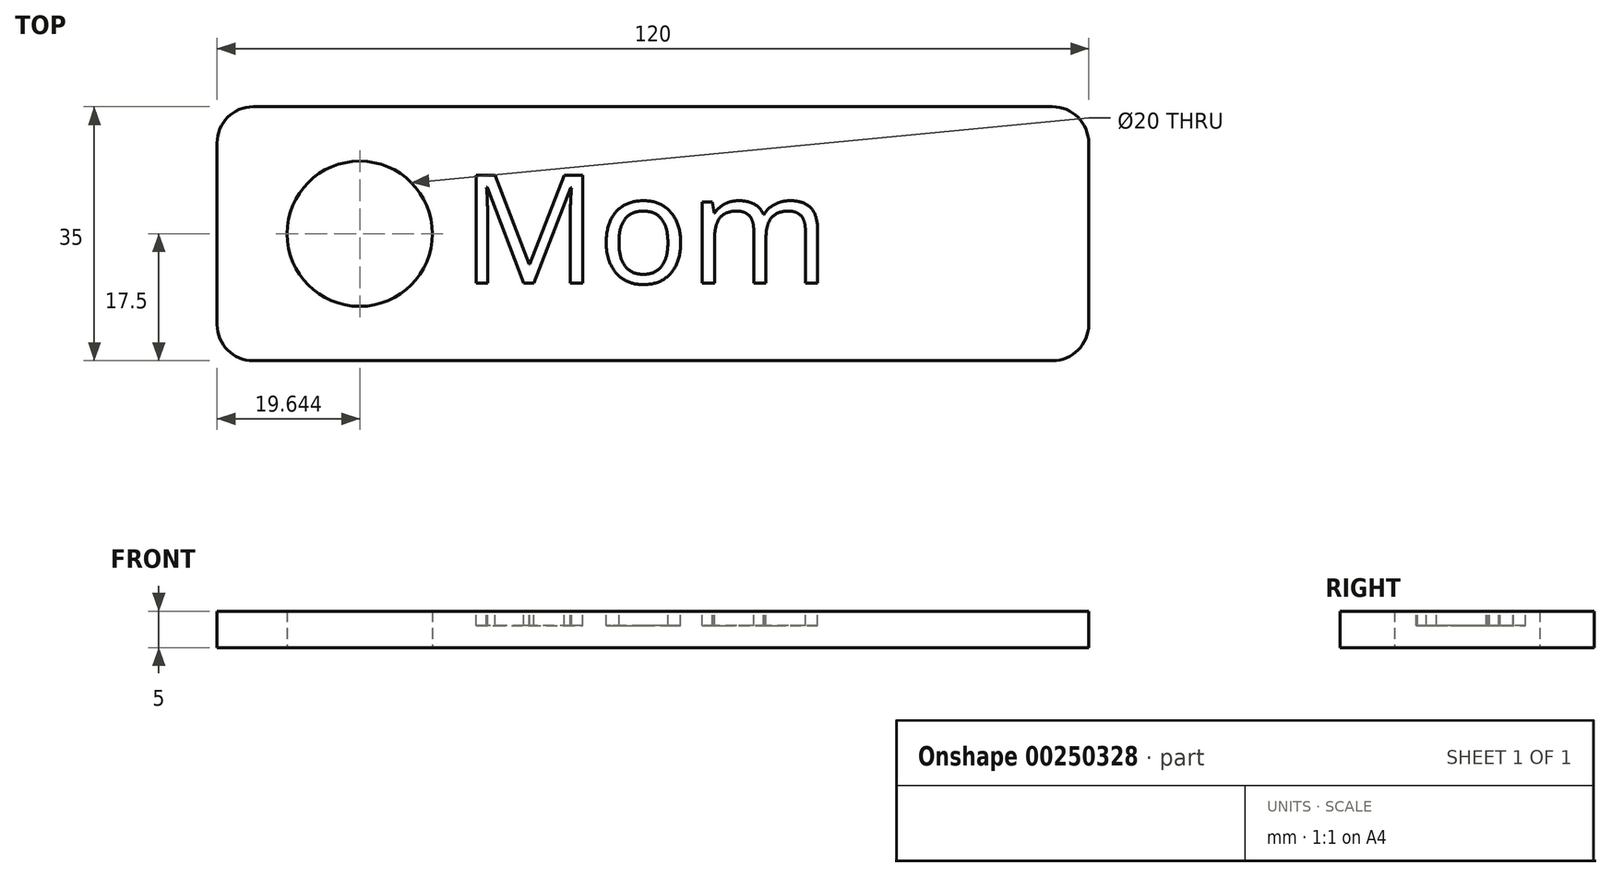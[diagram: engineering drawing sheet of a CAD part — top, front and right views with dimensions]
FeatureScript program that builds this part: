
annotation { "Feature Type Name" : "Feature", "Feature Type Description" : "" }
export const myFeature = defineFeature(function(context is Context, id is Id, definition is map)
    precondition{}
    {
        {
            var Q0;
            Q0=qCreatedBy(makeId("Top.planeOp"),FACE);
            var sketch = newSketch(context, id + "F0", { "sketchPlane" : qUnion([Q0])});
            skLineSegment(sketch, "E0.bottom", {"start": v(-60, 17.5) * mm, "end": v(60, 17.5) * mm});
            skLineSegment(sketch, "E0.top", {"start": v(-60, -17.5) * mm, "end": v(60, -17.5) * mm});
            skLineSegment(sketch, "E0.left", {"start": v(-60, 17.5) * mm, "end": v(-60, -17.5) * mm});
            skLineSegment(sketch, "E0.right", {"start": v(60, 17.5) * mm, "end": v(60, -17.5) * mm});
            skPoint(sketch, "E0.middle", {"position": v(0, 0) * mm});
            skCircle(sketch, "E1", {"center": v(-40.36, 0) * mm, "radius": 10 * mm});
            skSolve(sketch);
        }
        {
            var Q0;
            Q0=makeQuery(id+"F0.imprint","IMPRINT",FACE,{"disambiguationData":[TD([[makeQuery(id+"F0.imprint","IMPRINT",EDGE,{"derivedFrom":sQuery(id+"F0.wireOp",EDGE,"E0.bottom")}),-1.0]])]});
            extrude(context, id + "F1", {"entities" : qUnion([Q0]), "depth" : 5 * mm});
        }
        {
            var Q0;
            Q0=makeQuery(id+"F1.opExtrude","SWEPT_EDGE",EDGE,{"disambiguationData":[OSD([sQuery(id+"F0.wireOp",EDGE,"E0.top"),sQuery(id+"F0.wireOp",EDGE,"E0.left")])]});
            var Q1;
            Q1=makeQuery(id+"F1.opExtrude","SWEPT_EDGE",EDGE,{"disambiguationData":[OSD([sQuery(id+"F0.wireOp",EDGE,"E0.top"),sQuery(id+"F0.wireOp",EDGE,"E0.right")])]});
            var Q2;
            Q2=makeQuery(id+"F1.opExtrude","SWEPT_EDGE",EDGE,{"disambiguationData":[OSD([sQuery(id+"F0.wireOp",EDGE,"E0.bottom"),sQuery(id+"F0.wireOp",EDGE,"E0.right")])]});
            var Q3;
            Q3=makeQuery(id+"F1.opExtrude","SWEPT_EDGE",EDGE,{"disambiguationData":[OSD([sQuery(id+"F0.wireOp",EDGE,"E0.bottom"),sQuery(id+"F0.wireOp",EDGE,"E0.left")])]});
            fillet(context, id + "F2", {"entities" : qUnion([Q0, Q1, Q2, Q3]), "radius" : 5 * mm, "tangentPropagation" : true, "allowEdgeOverflow" : false});
        }
        {
            var Q0;
            Q0=makeQuery(id+"F1.opExtrude","CAP_FACE",FACE,{"disambiguationData":[OSD([sQuery(id+"F0.wireOp",EDGE,"E0.bottom"),sQuery(id+"F0.wireOp",EDGE,"E0.top"),sQuery(id+"F0.wireOp",EDGE,"E0.left"),sQuery(id+"F0.wireOp",EDGE,"E0.right"),sQuery(id+"F0.wireOp",EDGE,"E1")])],"isStart":false});
            var sketch = newSketch(context, id + "F3", { "sketchPlane" : qUnion([Q0])});
            skText(sketch, "E2", { "text": "Mom", "fontName": "OpenSans-Regular.ttf"});
            const initialGuessF3  = {"E2": [-0.0264, -0.0068, 1, 0, 0.015]};
            skSetInitialGuess(sketch, initialGuessF3);
            skSolve(sketch);
        }
        {
            var Q0;
            Q0 = qSketchRegion(id + "F3", true);
            extrude(context, id + "F4", {"entities" : qUnion([Q0]), "operationType" : NewBodyOperationType.REMOVE, "oppositeDirection" : true, "depth" : 2 * mm});
        }
    });
